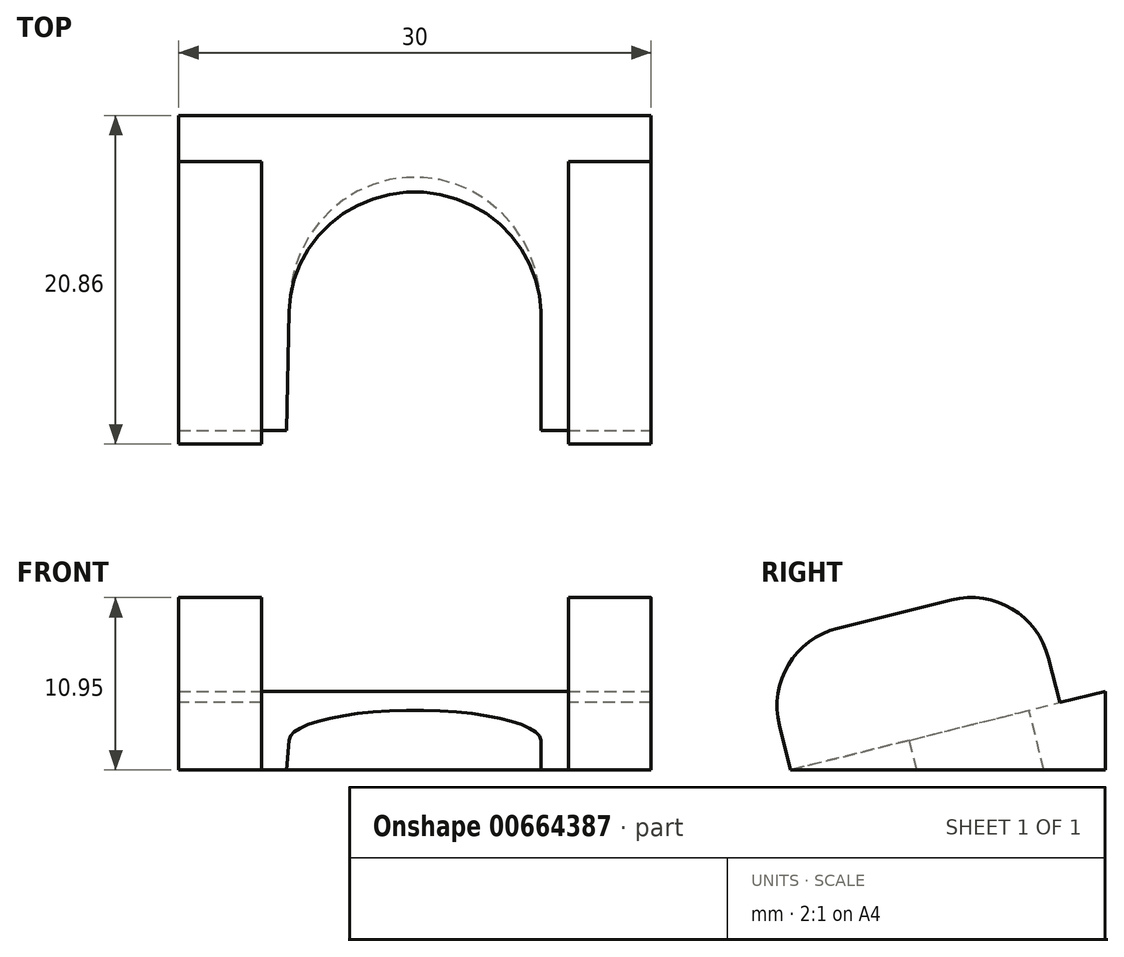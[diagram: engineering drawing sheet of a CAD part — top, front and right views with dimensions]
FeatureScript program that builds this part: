
annotation { "Feature Type Name" : "Feature", "Feature Type Description" : "" }
export const myFeature = defineFeature(function(context is Context, id is Id, definition is map)
    precondition{}
    {
        {
            var Q0;
            Q0=qCreatedBy(makeId("Top.planeOp"),FACE);
            var sketch = newSketch(context, id + "F0", { "sketchPlane" : qUnion([Q0])});
            skLineSegment(sketch, "E0.bottom", {"start": v(0, 0) * mm, "end": v(30, 0) * mm});
            skLineSegment(sketch, "E0.top", {"start": v(0, -20) * mm, "end": v(30, -20) * mm});
            skLineSegment(sketch, "E0.left", {"start": v(0, 0) * mm, "end": v(0, -20) * mm});
            skLineSegment(sketch, "E0.right", {"start": v(30, 0) * mm, "end": v(30, -20) * mm});
            skSolve(sketch);
        }
        {
            var Q0;
            Q0 = qSketchRegion(id + "F0", true);
            extrude(context, id + "F1", {"entities" : qUnion([Q0]), "depth" : 5 * mm, "offsetDistance" : 25.4 * mm});
        }
        {
            var Q0;
            Q0=makeQuery(id+"F1.opExtrude","SWEPT_FACE",FACE,{"disambiguationData":[OSD([sQuery(id+"F0.wireOp",EDGE,"E0.right")])]});
            var sketch = newSketch(context, id + "F2", { "sketchPlane" : qUnion([Q0])});
            skLineSegment(sketch, "E1", {"start": v(-20, 0) * mm, "end": v(0, 5) * mm});
            skLineSegment(sketch, "E2", {"start": v(0, 5) * mm, "end": v(0, 0) * mm});
            skLineSegment(sketch, "E3", {"start": v(0, 0) * mm, "end": v(-20, 0) * mm});
            skSolve(sketch);
        }
        {
            var Q0;
            Q0=makeQuery(id+"F2.imprint","IMPRINT",FACE,{"disambiguationData":[TD([[makeQuery(id+"F2.imprint","IMPRINT",EDGE,{"derivedFrom":sQuery(id+"F2.wireOp",EDGE,"E1")}),1.0]])]});
            extrude(context, id + "F3", {"entities" : qUnion([Q0]), "operationType" : NewBodyOperationType.REMOVE, "endBound" : BoundingType.UP_TO_NEXT, "oppositeDirection" : true, "depth" : 25.4 * mm, "offsetDistance" : 25.4 * mm});
        }
        {
            var Q0;
            Q0=makeQuery(id+"F3.boolean.opBoolean","COPY",FACE,{"derivedFrom":makeQuery(id+"F3.opExtrude","SWEPT_FACE",FACE,{"disambiguationData":[OSD([sQuery(id+"F2.wireOp",EDGE,"E1")])]})});
            var sketch = newSketch(context, id + "F4", { "sketchPlane" : qUnion([Q0])});
            skArc(sketch, "E4", {"start": v(23, -11.94) * mm, "mid": v(15.16, -3.79) * mm, "end": v(7, -11.63) * mm});
            skPoint(sketch, "E4.first.point", {"position": v(15, -3.79) * mm});
            skPoint(sketch, "E4.first.point.positionSnap0", {"position": v(15, 1.21) * mm});
            skPoint(sketch, "E4.second.point", {"position": v(15, -19.79) * mm});
            skPoint(sketch, "E4.second.point.positionSnap0", {"position": v(15, 1.21) * mm});
            skPoint(sketch, "E4.third.point", {"position": v(7, -11.63) * mm});
            skLineSegment(sketch, "E5", {"start": v(7, -11.63) * mm, "end": v(6.85, -19.4) * mm});
            skLineSegment(sketch, "E6", {"start": v(23, -11.63) * mm, "end": v(23, -19.4) * mm});
            skSolve(sketch);
        }
        {
            var Q0;
            {var subQ7=sQuery(id+"F4.wireOp",EDGE,"E5");Q0=makeQuery(id+"F4.imprint","IMPRINT",FACE,{"disambiguationData":[TD([[makeQuery(id+"F4.imprint","IMPRINT",EDGE,{"derivedFrom":subQ7}),1.0]])]});}
            extrude(context, id + "F5", {"entities" : qUnion([Q0]), "operationType" : NewBodyOperationType.REMOVE, "oppositeDirection" : true, "depth" : 25.4 * mm, "offsetDistance" : 25.4 * mm});
        }
        {
            var Q0;
            Q0=makeQuery(id+"F3.boolean.opBoolean","COPY",FACE,{"derivedFrom":makeQuery(id+"F3.opExtrude","SWEPT_FACE",FACE,{"disambiguationData":[OSD([sQuery(id+"F2.wireOp",EDGE,"E1")])]})});
            var sketch = newSketch(context, id + "F6", { "sketchPlane" : qUnion([Q0])});
            skLineSegment(sketch, "E7.bottom", {"start": v(24.75, -19.4) * mm, "end": v(5.25, -19.4) * mm});
            skLineSegment(sketch, "E7.top", {"start": v(24.75, 1.21) * mm, "end": v(5.25, 1.21) * mm});
            skLineSegment(sketch, "E7.left", {"start": v(24.75, -19.4) * mm, "end": v(24.75, 1.21) * mm});
            skLineSegment(sketch, "E7.right", {"start": v(5.25, -19.4) * mm, "end": v(5.25, 1.21) * mm});
            skLineSegment(sketch, "E8", {"start": v(5.25, -19.4) * mm, "end": v(0, -19.4) * mm});
            skLineSegment(sketch, "E9", {"start": v(0, -19.4) * mm, "end": v(0, 1.21) * mm});
            skLineSegment(sketch, "E10", {"start": v(0, 1.21) * mm, "end": v(5.25, 1.21) * mm});
            skLineSegment(sketch, "E11", {"start": v(24.75, -19.4) * mm, "end": v(30, -19.4) * mm});
            skLineSegment(sketch, "E12", {"start": v(30, -19.4) * mm, "end": v(30, 1.21) * mm});
            skLineSegment(sketch, "E13", {"start": v(30, 1.21) * mm, "end": v(24.75, 1.21) * mm});
            skLineSegment(sketch, "E14", {"start": v(30, -1.79) * mm, "end": v(0, -1.79) * mm});
            skSolve(sketch);
        }
        {
            var Q0;
            {var subQ0=sQuery(id+"F6.wireOp",EDGE,"E11");Q0=makeQuery(id+"F6.imprint","IMPRINT",FACE,{"disambiguationData":[TD([[makeQuery(id+"F6.imprint","IMPRINT",EDGE,{"derivedFrom":subQ0}),1.0]])]});}
            var Q1;
            {var subQ0=sQuery(id+"F6.wireOp",EDGE,"E8");Q1=makeQuery(id+"F6.imprint","IMPRINT",FACE,{"disambiguationData":[TD([[makeQuery(id+"F6.imprint","IMPRINT",EDGE,{"derivedFrom":subQ0}),1.0]])]});}
            extrude(context, id + "F7", {"entities" : qUnion([Q0, Q1]), "operationType" : NewBodyOperationType.ADD, "depth" : 8 * mm, "offsetDistance" : 25.4 * mm});
        }
        {
            var Q0;
            {var subQ0=sQuery(id+"F6.wireOp",EDGE,"E14");Q0=makeQuery(id+"F7.opExtrude","CAP_EDGE",EDGE,{"disambiguationData":[OSD([subQ0]),TDD([makeQuery(id+"F6.imprint","IMPRINT",EDGE,{"disambiguationData":[TD([[makeQuery(id+"F6.imprint","INTERSECT",VERTEX,{"derivedFrom":[sQuery(id+"F6.wireOp",EDGE,"E9"),subQ0]}),1.0]])],"derivedFrom":subQ0})])],"isStart":false});}
            var Q1;
            {var subQ0=sQuery(id+"F6.wireOp",EDGE,"E14");Q1=makeQuery(id+"F7.opExtrude","CAP_EDGE",EDGE,{"disambiguationData":[OSD([subQ0]),TDD([makeQuery(id+"F6.imprint","IMPRINT",EDGE,{"disambiguationData":[TD([[makeQuery(id+"F6.imprint","INTERSECT",VERTEX,{"derivedFrom":[sQuery(id+"F6.wireOp",EDGE,"E12"),subQ0]}),-1.0]])],"derivedFrom":subQ0})])],"isStart":false});}
            var Q2;
            Q2=makeQuery(id+"F7.opExtrude","CAP_EDGE",EDGE,{"disambiguationData":[OSD([sQuery(id+"F6.wireOp",EDGE,"E8")])],"isStart":false});
            var Q3;
            Q3=makeQuery(id+"F7.opExtrude","CAP_EDGE",EDGE,{"disambiguationData":[OSD([sQuery(id+"F6.wireOp",EDGE,"E11")])],"isStart":false});
            fillet(context, id + "F8", {"entities" : qUnion([Q0, Q1, Q2, Q3]), "radius" : 5.08 * mm, "tangentPropagation" : true, "allowEdgeOverflow" : false});
        }
    });
